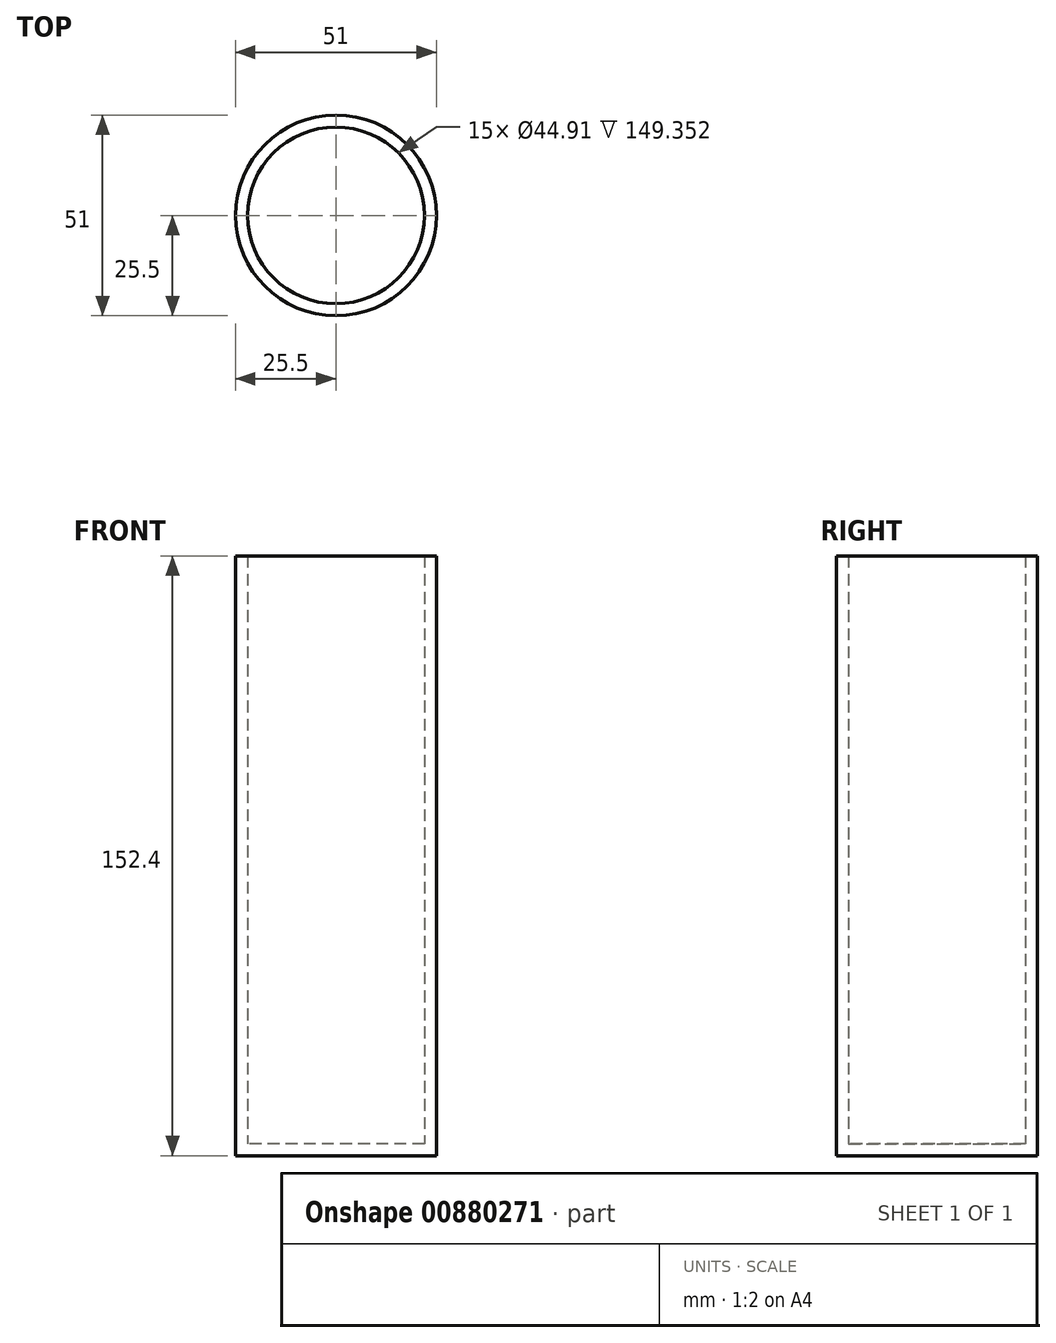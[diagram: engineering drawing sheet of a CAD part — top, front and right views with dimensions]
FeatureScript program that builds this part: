
annotation { "Feature Type Name" : "Feature", "Feature Type Description" : "" }
export const myFeature = defineFeature(function(context is Context, id is Id, definition is map)
    precondition{}
    {
        {
            var Q0;
            Q0=qCreatedBy(makeId("Top.planeOp"),FACE);
            var sketch = newSketch(context, id + "F0", { "sketchPlane" : qUnion([Q0])});
            skCircle(sketch, "E0", {"center": v(0, 0) * mm, "radius": 25.5 * mm});
            skSolve(sketch);
        }
        {
            var Q0;
            Q0 = qSketchRegion(id + "F0", true);
            extrude(context, id + "F1", {"entities" : qUnion([Q0]), "depth" : 152.4 * mm, "offsetDistance" : 25.4 * mm});
        }
        {
            var Q0;
            Q0=makeQuery(id+"F1.opExtrude","CAP_FACE",FACE,{"disambiguationData":[OSD([sQuery(id+"F0.wireOp",EDGE,"E0")])],"isStart":false});
            var Q1;
            Q1=makeQuery(id+"F1.opExtrude","SWEPT_BODY",BODY,{"disambiguationData":[OSD([sQuery(id+"F0.wireOp",EDGE,"E0")])]});
            shell(context, id + "F2", {"entities" : qUnion([Q0]), "parts" : qUnion([Q1]), "thickness" : 3.05 * mm});
        }
    });
